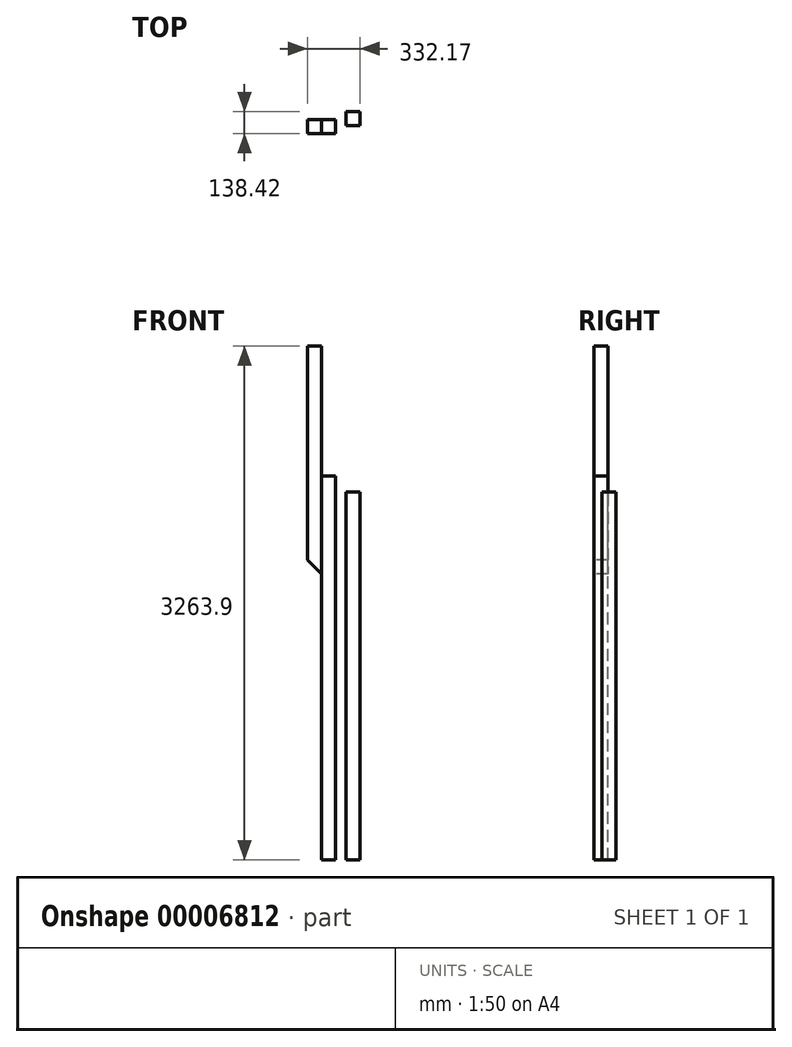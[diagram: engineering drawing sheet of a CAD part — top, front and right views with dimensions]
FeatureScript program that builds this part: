
annotation { "Feature Type Name" : "Feature", "Feature Type Description" : "" }
export const myFeature = defineFeature(function(context is Context, id is Id, definition is map)
    precondition{}
    {
        {
            var Q0;
            Q0=qCreatedBy(makeId("Front.planeOp"),FACE);
            var sketch = newSketch(context, id + "F0", { "sketchPlane" : qUnion([Q0])});
            skLineSegment(sketch, "E0.bottom", {"start": v(-155.62, 0) * mm, "end": v(-66.72, 0) * mm});
            skLineSegment(sketch, "E0.top", {"start": v(-155.62, 2438.4) * mm, "end": v(-66.72, 2438.4) * mm});
            skLineSegment(sketch, "E0.left", {"start": v(-155.62, 0) * mm, "end": v(-155.62, 2438.4) * mm});
            skLineSegment(sketch, "E0.right", {"start": v(-66.72, 0) * mm, "end": v(-66.72, 2438.4) * mm});
            skSolve(sketch);
        }
        {
            var Q0;
            Q0 = qSketchRegion(id + "F0", true);
            extrude(context, id + "F1", {"entities" : qUnion([Q0]), "depth" : 88.9 * mm});
        }
        {
            var Q0;
            Q0=makeQuery(id+"F1.opExtrude","CAP_FACE",FACE,{"disambiguationData":[OSD([sQuery(id+"F0.wireOp",EDGE,"E0.bottom"),sQuery(id+"F0.wireOp",EDGE,"E0.top"),sQuery(id+"F0.wireOp",EDGE,"E0.left"),sQuery(id+"F0.wireOp",EDGE,"E0.right")])],"isStart":false});
            var sketch = newSketch(context, id + "F2", { "sketchPlane" : qUnion([Q0])});
            skLineSegment(sketch, "E1", {"start": v(-155.62, 1816.1) * mm, "end": v(-155.62, 3263.9) * mm});
            skLineSegment(sketch, "E2", {"start": v(-155.62, 3263.9) * mm, "end": v(-244.52, 3263.9) * mm});
            skLineSegment(sketch, "E3", {"start": v(-244.52, 3263.9) * mm, "end": v(-244.52, 1905) * mm});
            skLineSegment(sketch, "E4", {"start": v(-244.52, 1905) * mm, "end": v(-155.62, 1816.1) * mm});
            skSolve(sketch);
        }
        {
            var Q0;
            Q0 = qSketchRegion(id + "F2", true);
            var Q1;
            Q1=makeQuery(id+"F1.opExtrude","CAP_FACE",FACE,{"disambiguationData":[OSD([sQuery(id+"F0.wireOp",EDGE,"E0.bottom"),sQuery(id+"F0.wireOp",EDGE,"E0.top"),sQuery(id+"F0.wireOp",EDGE,"E0.left"),sQuery(id+"F0.wireOp",EDGE,"E0.right")])],"isStart":true});
            extrude(context, id + "F3", {"entities" : qUnion([Q0]), "endBound" : BoundingType.UP_TO_SURFACE, "oppositeDirection" : true, "endBoundEntityFace" : qUnion([Q1]), "depth" : 25.4 * mm});
        }
        {
            var Q0;
            Q0=qCreatedBy(makeId("Top.planeOp"),FACE);
            var sketch = newSketch(context, id + "F4", { "sketchPlane" : qUnion([Q0])});
            skLineSegment(sketch, "E5.bottom", {"start": v(-1.25, 49.52) * mm, "end": v(87.65, 49.52) * mm});
            skLineSegment(sketch, "E5.top", {"start": v(-1.25, -39.38) * mm, "end": v(87.65, -39.38) * mm});
            skLineSegment(sketch, "E5.left", {"start": v(-1.25, 49.52) * mm, "end": v(-1.25, -39.38) * mm});
            skLineSegment(sketch, "E5.right", {"start": v(87.65, 49.52) * mm, "end": v(87.65, -39.38) * mm});
            skSolve(sketch);
        }
        {
            var Q0;
            Q0 = qSketchRegion(id + "F4", true);
            extrude(context, id + "F5", {"entities" : qUnion([Q0]), "depth" : 2336.8 * mm});
        }
    });
